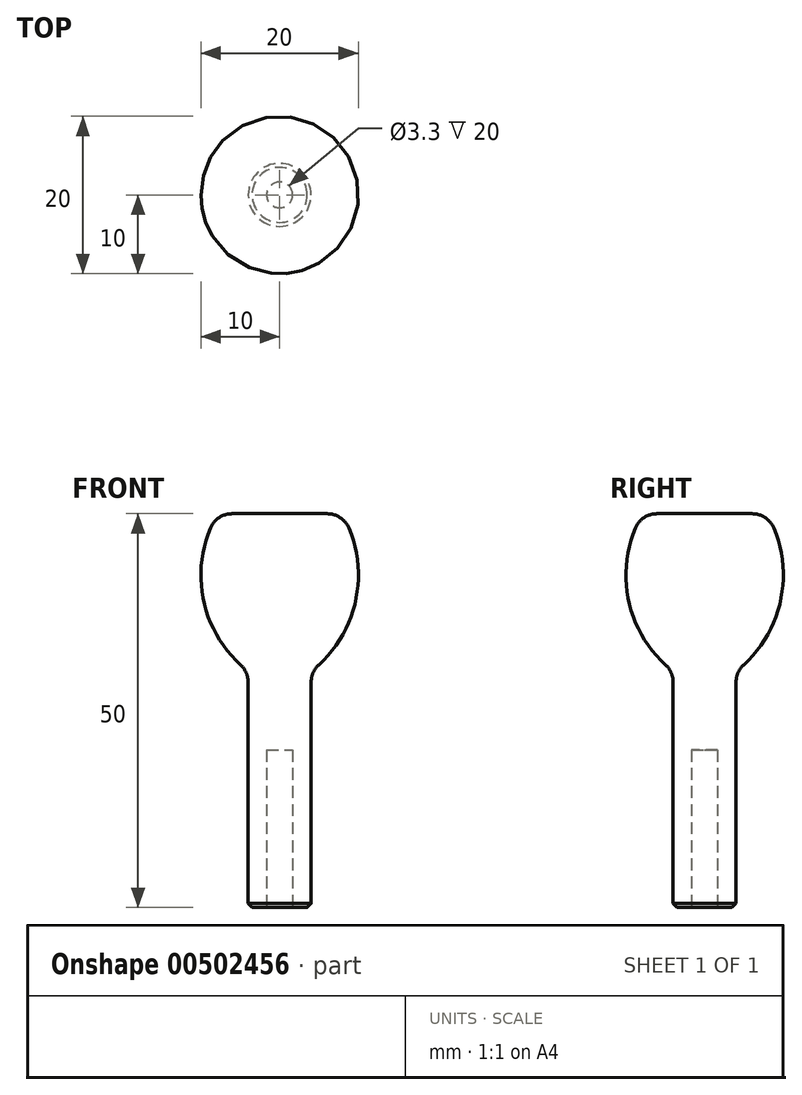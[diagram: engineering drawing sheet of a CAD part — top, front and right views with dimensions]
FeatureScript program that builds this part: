
annotation { "Feature Type Name" : "Feature", "Feature Type Description" : "" }
export const myFeature = defineFeature(function(context is Context, id is Id, definition is map)
    precondition{}
    {
        {
            var Q0;
            Q0=qCreatedBy(makeId("Front.planeOp"),FACE);
            var sketch = newSketch(context, id + "F0", { "sketchPlane" : qUnion([Q0])});
            skLineSegment(sketch, "E0", {"start": v(0, 84.4) * mm, "end": v(0, 0) * mm, "construction": true});
            skLineSegment(sketch, "E1", {"start": v(0, 0) * mm, "end": v(4, 0) * mm});
            skLineSegment(sketch, "E2", {"start": v(4, 0) * mm, "end": v(4, 30) * mm});
            skLineSegment(sketch, "E3", {"start": v(0, 50) * mm, "end": v(7.88, 50) * mm});
            skArc(sketch, "E4", {"start": v(4, 30) * mm, "mid": v(9.72, 39.27) * mm, "end": v(7.88, 50) * mm});
            skLineSegment(sketch, "E5", {"start": v(0, 50) * mm, "end": v(0, 0) * mm});
            skPoint(sketch, "E6", {"position": v(0, 42.2) * mm});
            skSolve(sketch);
        }
        {
            var Q0;
            Q0=makeQuery(id+"F0.imprint","IMPRINT",FACE,{"disambiguationData":[TD([[makeQuery(id+"F0.imprint","IMPRINT",EDGE,{"derivedFrom":sQuery(id+"F0.wireOp",EDGE,"E1")}),1.0]])]});
            var Q1;
            Q1=sQuery(id+"F0.wireOp",EDGE,"E0");
            revolve(context, id + "F1", {"entities" : qUnion([Q0]), "axis" : qUnion([Q1]), "revolveType" : RevolveType.FULL});
        }
        {
            var Q0;
            Q0=makeQuery(id+"F1.opRevolve","SWEPT_EDGE",EDGE,{"disambiguationData":[OSD([sQuery(id+"F0.wireOp",EDGE,"E3"),sQuery(id+"F0.wireOp",EDGE,"E4")])]});
            var Q1;
            Q1=makeQuery(id+"F1.opRevolve","SWEPT_EDGE",EDGE,{"disambiguationData":[OSD([sQuery(id+"F0.wireOp",EDGE,"E2"),sQuery(id+"F0.wireOp",EDGE,"E4")])]});
            fillet(context, id + "F2", {"entities" : qUnion([Q0, Q1]), "radius" : 3 * mm, "tangentPropagation" : true, "allowEdgeOverflow" : false});
        }
        {
            var Q0;
            Q0=makeQuery(id+"F1.opRevolve","SWEPT_FACE",FACE,{"disambiguationData":[OSD([sQuery(id+"F0.wireOp",EDGE,"E1")])]});
            var sketch = newSketch(context, id + "F3", { "sketchPlane" : qUnion([Q0])});
            skCircle(sketch, "E7", {"center": v(0, 0) * mm, "radius": 1.65 * mm});
            skSolve(sketch);
        }
        {
            var Q0;
            Q0=makeQuery(id+"F3.imprint","IMPRINT",FACE,{"disambiguationData":[TD([[makeQuery(id+"F3.imprint","IMPRINT",EDGE,{"derivedFrom":sQuery(id+"F3.wireOp",EDGE,"E7")}),1.0]])]});
            extrude(context, id + "F4", {"entities" : qUnion([Q0]), "operationType" : NewBodyOperationType.REMOVE, "oppositeDirection" : true, "depth" : 20 * mm, "offsetDistance" : 25 * mm});
        }
        {
            var Q0;
            Q0=makeQuery(id+"F4.boolean.opBoolean","COPY",EDGE,{"derivedFrom":makeQuery(id+"F4.opExtrude","CAP_EDGE",EDGE,{"disambiguationData":[OSD([sQuery(id+"F3.wireOp",EDGE,"E7")])],"isStart":true})});
            var Q1;
            Q1=makeQuery(id+"F1.opRevolve","SWEPT_EDGE",EDGE,{"disambiguationData":[OSD([sQuery(id+"F0.wireOp",EDGE,"E1"),sQuery(id+"F0.wireOp",EDGE,"E2")])]});
            chamfer(context, id + "F5", {"entities" : qUnion([Q0, Q1]), "width" : 0.5 * mm, "tangentPropagation" : true});
        }
    });
